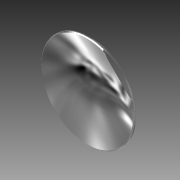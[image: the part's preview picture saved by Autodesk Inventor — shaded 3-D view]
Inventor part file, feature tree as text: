
AUTODESK INVENTOR PART (.ipt)
format: ipt  version: 2014 (Build 180170000, 170)  size: 110,592 bytes
history: native  units: mm (DEFAULTED — no unit token found)
features: sketch x3, plane x3, extrude x2, chamfer x2, reference x2
ambient origin geometry x8: Origin, YZ Plane, XZ Plane, XY Plane, X Axis, Y Axis, Z Axis, Center Point
bodies: Solid1 (feature_tree)
feature tree (12):
  sketch  "Sketch1"  dims[d2=25.4mm d3=0.0mm d4=0.127mm d5=0.127mm d6=25.4mm d7=0.0mm]
  plane  "Work Plane1"
  plane  "Work Plane2"
  extrude  "Extrusion1"  Depth=0.127mm
  chamfer  "Chamfer1"  Distance=25.4mm
  plane  "Work Plane3"
  extrude  "Extrusion2"  TaperAngle=45.0deg  [1 undecoded]
  chamfer  "Chamfer2"  [1 undecoded]
  sketch  "Sketch2"  dims[d8=0.127mm d9=0.127mm d10=45.0deg d11=45.0deg]
  reference  "Reference1"
  sketch  "Sketch3"
  reference  "Reference2"
note: 2 required parameter values undecoded (feature->parameter linkage not recoverable at this tier; creation-order binding heuristic only, values carry confidence <= 0.55)
